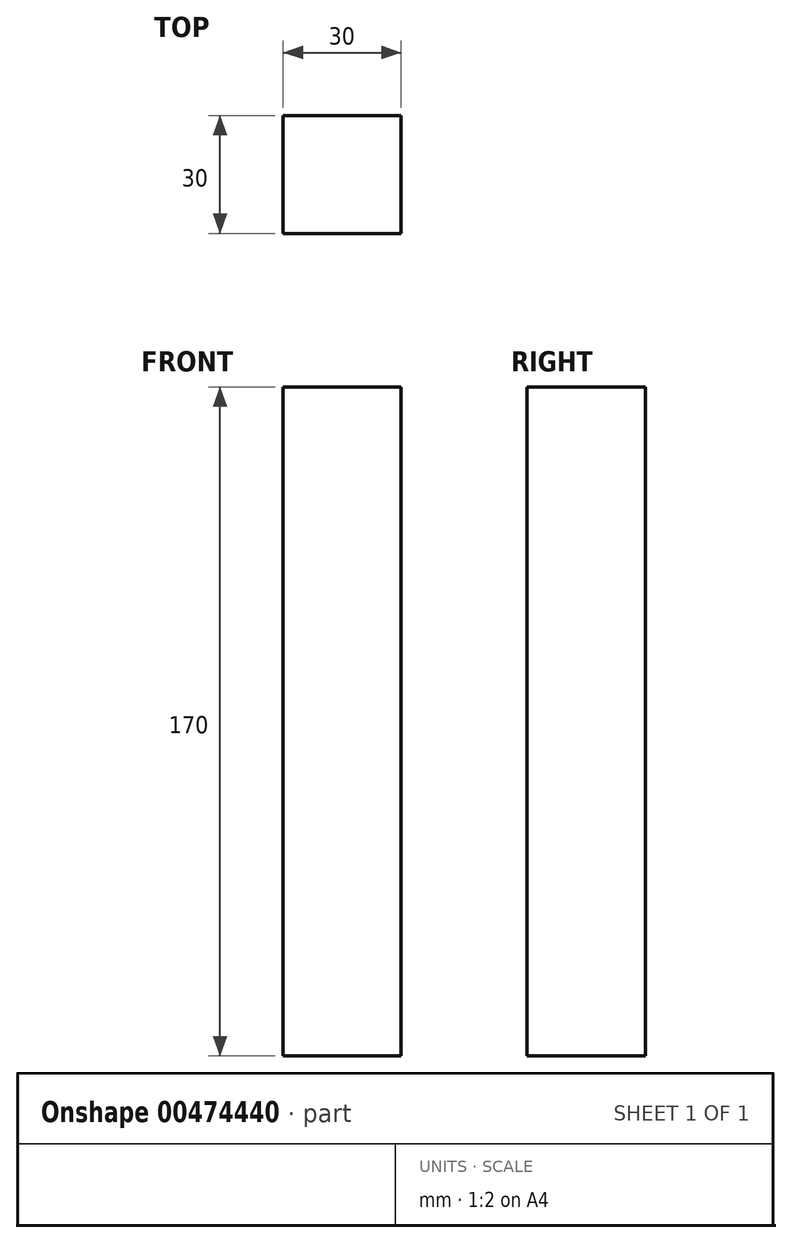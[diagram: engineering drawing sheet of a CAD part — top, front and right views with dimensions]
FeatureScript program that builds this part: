
annotation { "Feature Type Name" : "Feature", "Feature Type Description" : "" }
export const myFeature = defineFeature(function(context is Context, id is Id, definition is map)
    precondition{}
    {
        {
            var Q0;
            Q0=qCreatedBy(makeId("Right.planeOp"),FACE);
            var sketch = newSketch(context, id + "F0", { "sketchPlane" : qUnion([Q0])});
            skLineSegment(sketch, "E0.bottom", {"start": v(0, 0) * mm, "end": v(30, 0) * mm});
            skLineSegment(sketch, "E0.top", {"start": v(0, 170) * mm, "end": v(30, 170) * mm});
            skLineSegment(sketch, "E0.left", {"start": v(0, 0) * mm, "end": v(0, 170) * mm});
            skLineSegment(sketch, "E0.right", {"start": v(30, 0) * mm, "end": v(30, 170) * mm});
            skSolve(sketch);
        }
        {
            var Q0;
            Q0 = qSketchRegion(id + "F0", true);
            extrude(context, id + "F1", {"entities" : qUnion([Q0]), "depth" : 30 * mm, "offsetDistance" : 25 * mm});
        }
    });
